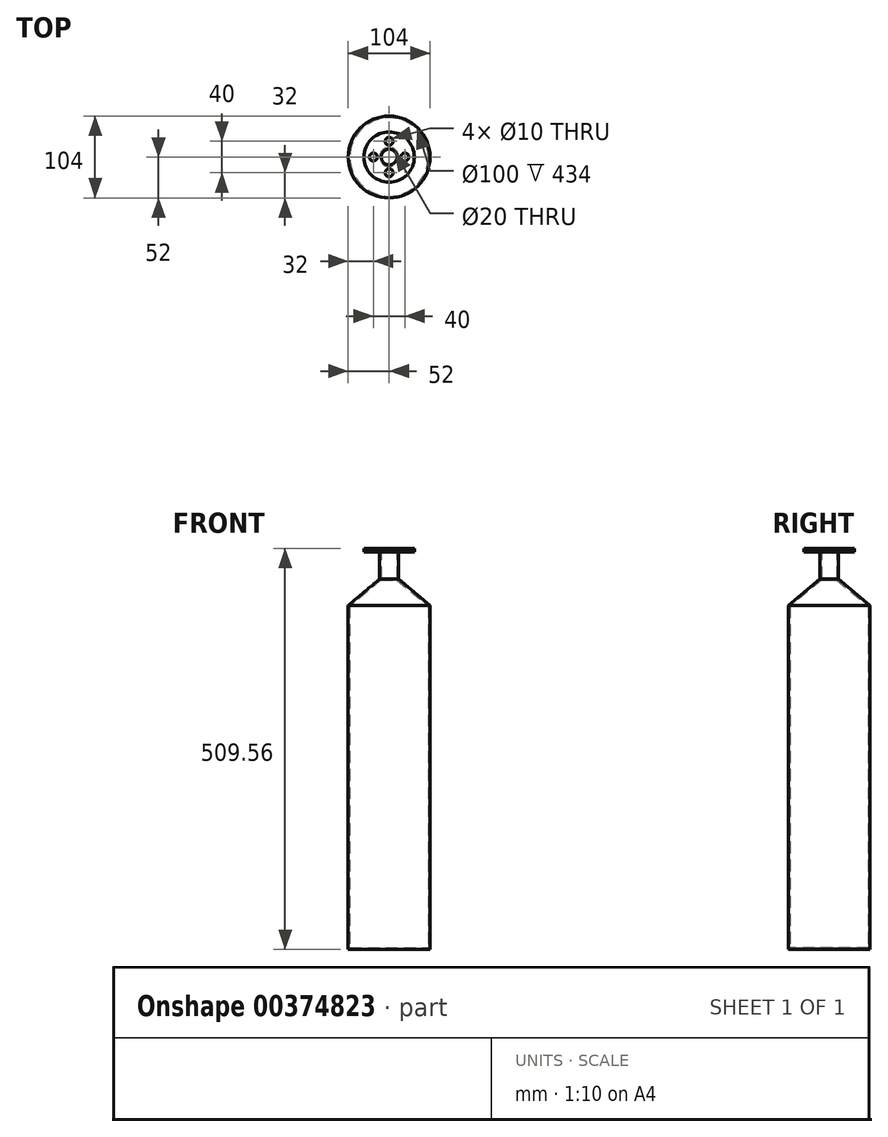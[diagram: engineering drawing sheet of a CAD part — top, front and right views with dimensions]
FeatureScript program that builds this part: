
annotation { "Feature Type Name" : "Feature", "Feature Type Description" : "" }
export const myFeature = defineFeature(function(context is Context, id is Id, definition is map)
    precondition{}
    {
        {
            var Q0;
            Q0=qCreatedBy(makeId("Front.planeOp"),FACE);
            var sketch = newSketch(context, id + "F0", { "sketchPlane" : qUnion([Q0])});
            skLineSegment(sketch, "E0", {"start": v(-50, 434) * mm, "end": v(-50, 0) * mm});
            skLineSegment(sketch, "E1", {"start": v(-50, 0) * mm, "end": v(0, 0) * mm});
            skLineSegment(sketch, "E2", {"start": v(0, 0) * mm, "end": v(0, 432.05) * mm, "construction": true});
            skLineSegment(sketch, "E3", {"start": v(0, 0) * mm, "end": v(0, -2) * mm});
            skLineSegment(sketch, "E4", {"start": v(-50, 434) * mm, "end": v(-10, 467.56) * mm});
            skPoint(sketch, "E5.start.orphan", {"position": v(-10, 503.08) * mm});
            skPoint(sketch, "E6.start.orphan", {"position": v(-10, 432.05) * mm});
            skLineSegment(sketch, "E7", {"start": v(-10, 467.56) * mm, "end": v(-10, 507.56) * mm});
            skLineSegment(sketch, "E8.0", {"start": v(-12, 468.5) * mm, "end": v(-12, 507.56) * mm});
            skLineSegment(sketch, "E8.1", {"start": v(-52, 434.93) * mm, "end": v(-12, 468.5) * mm});
            skLineSegment(sketch, "E8.2", {"start": v(-52, 434.93) * mm, "end": v(-52, -2) * mm});
            skLineSegment(sketch, "E8.3", {"start": v(-52, -2) * mm, "end": v(0, -2) * mm});
            skLineSegment(sketch, "E9", {"start": v(-12, 507.56) * mm, "end": v(-10, 507.56) * mm});
            skSolve(sketch);
        }
        {
            var Q0;
            Q0=qSketchRegion(id+"F0",true);
            var Q1;
            Q1=sQuery(id+"F0.wireOp",EDGE,"E2");
            revolve(context, id + "F1", {"entities" : qUnion([Q0]), "axis" : qUnion([Q1]), "revolveType" : RevolveType.FULL});
        }
        {
            var Q0;
            Q0=makeQuery(id+"F1.opRevolve","SWEPT_FACE",FACE,{"disambiguationData":[OSD([sQuery(id+"F0.wireOp",EDGE,"E9")])]});
            var sketch = newSketch(context, id + "F2", { "sketchPlane" : qUnion([Q0])});
            skCircle(sketch, "E10", {"center": v(0, 0) * mm, "radius": 32 * mm});
            skSolve(sketch);
        }
        {
            var Q0;
            Q0=makeQuery(id+"F2.imprint","IMPRINT",FACE,{"disambiguationData":[TD([[makeQuery(id+"F2.imprint","IMPRINT",EDGE,{"derivedFrom":sQuery(id+"F2.wireOp",EDGE,"E10")}),1.0]])]});
            extrude(context, id + "F3", {"entities" : qUnion([Q0]), "operationType" : NewBodyOperationType.ADD, "oppositeDirection" : true, "depth" : 5 * mm});
        }
        {
            var Q0;
            {var subQ0=sQuery(id+"F0.wireOp",EDGE,"E9");Q0=makeQuery(id+"F3.boolean.opBoolean","MERGE",FACE,{"derivedFrom":[makeQuery(id+"F1.opRevolve","SWEPT_FACE",FACE,{"disambiguationData":[OSD([subQ0])]}),makeQuery(id+"F3.opExtrude","CAP_FACE",FACE,{"disambiguationData":[OSD([sQuery(id+"F0.wireOp",EDGE,"E8.0"),subQ0,sQuery(id+"F2.wireOp",EDGE,"E10")])],"isStart":true})]});}
            var sketch = newSketch(context, id + "F4", { "sketchPlane" : qUnion([Q0])});
            skCircle(sketch, "E11", {"center": v(0, 20) * mm, "radius": 5 * mm});
            skCircle(sketch, "E12.1.0", {"center": v(-20, 0) * mm, "radius": 5 * mm});
            skCircle(sketch, "E12.2.0", {"center": v(0, -20) * mm, "radius": 5 * mm});
            skPoint(sketch, "E12.center", {"position": v(0, 0) * mm});
            skCircle(sketch, "E13.1.3.0", {"center": v(20, 0) * mm, "radius": 5 * mm});
            skSolve(sketch);
        }
        {
            var Q0;
            Q0=qSketchRegion(id+"F4",true);
            var Q1;
            Q1=makeQuery(id+"F3.opExtrude","CAP_FACE",FACE,{"disambiguationData":[OSD([sQuery(id+"F0.wireOp",EDGE,"E8.0"),sQuery(id+"F0.wireOp",EDGE,"E9"),sQuery(id+"F2.wireOp",EDGE,"E10")])],"isStart":false});
            extrude(context, id + "F5", {"entities" : qUnion([Q0]), "operationType" : NewBodyOperationType.REMOVE, "endBound" : BoundingType.UP_TO_SURFACE, "oppositeDirection" : true, "endBoundEntityFace" : qUnion([Q1]), "depth" : 25 * mm});
        }
    });
